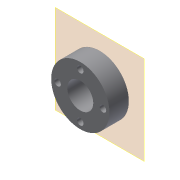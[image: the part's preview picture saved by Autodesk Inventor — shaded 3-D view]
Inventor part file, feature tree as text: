
AUTODESK INVENTOR PART (.ipt)
format: ipt  version: 2017 (Build 210142000, 142)  size: 94,208 bytes
history: native  units: in
note: dims shown in document units (in); Inventor stores cm internally (conversion verified against a paired STEP export)
features: reference x5, other x2, plane x1, extrude x1, sketch x1
ambient origin geometry x8: Origin, YZ Plane, XZ Plane, XY Plane, X Axis, Y Axis, Z Axis, Center Point
bodies: Solid1 (feature_tree)
feature tree (10):
  plane  "Work Plane1"
  extrude  "Extrusion1"  Depth=1.5in TaperAngle=0.0deg
  sketch  "Sketch1"  dims[d0=4.5in d1=1.5in d2=0.0in]
  reference  "Reference1"
  reference  "Reference2"
  reference  "Reference3"
  reference  "Reference4"
  reference  "Reference5"
  other  "Assembly7"
  other  "Base:1"
